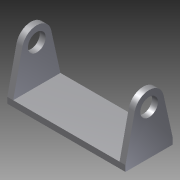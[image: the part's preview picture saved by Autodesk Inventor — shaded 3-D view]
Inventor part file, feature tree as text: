
AUTODESK INVENTOR PART (.ipt)
format: ipt  version: 2012 (Build 160160000, 160)  size: 109,568 bytes
history: native  units: in
note: dims shown in document units (in); Inventor stores cm internally (conversion verified against a paired STEP export)
features: extrude x2, sketch x2
ambient origin geometry x8: Origin, YZ Plane, XZ Plane, XY Plane, X Axis, Y Axis, Z Axis, Center Point
bodies: Solid1 (feature_tree)
feature tree (4):
  extrude  "Extrusion1"  Depth=2.5in
  extrude  "Extrusion2"  Depth=0.125in
  sketch  "Sketch1"  dims[d0=1.25in d1=2.5in]
  sketch  "Sketch2"  dims[d2=0.125in d3=0.125in d4=0.125in d5=1.0in d6=0.0in d7=0.625in d8=0.125in d9=0.375in d10=0.5in d11=1.0in d12=0.0in]
